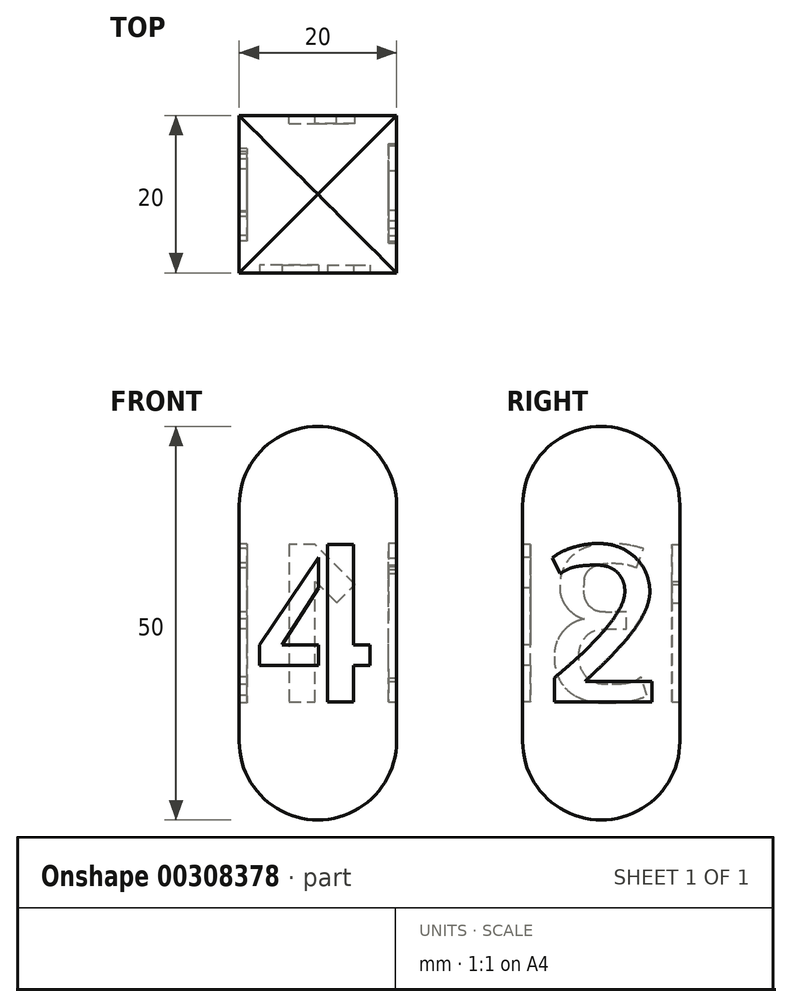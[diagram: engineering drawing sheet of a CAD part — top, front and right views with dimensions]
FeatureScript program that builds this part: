
annotation { "Feature Type Name" : "Feature", "Feature Type Description" : "" }
export const myFeature = defineFeature(function(context is Context, id is Id, definition is map)
    precondition{}
    {
        {
            var Q0;
            Q0=qCreatedBy(makeId("Top.planeOp"),FACE);
            var sketch = newSketch(context, id + "F0", { "sketchPlane" : qUnion([Q0])});
            skLineSegment(sketch, "E0.bottom", {"start": v(0, 0) * mm, "end": v(-20, 0) * mm});
            skLineSegment(sketch, "E0.top", {"start": v(0, 20) * mm, "end": v(-20, 20) * mm});
            skLineSegment(sketch, "E0.left", {"start": v(0, 0) * mm, "end": v(0, 20) * mm});
            skLineSegment(sketch, "E0.right", {"start": v(-20, 0) * mm, "end": v(-20, 20) * mm});
            skSolve(sketch);
        }
        {
            var Q0;
            Q0=makeQuery(id+"F0.imprint","IMPRINT",FACE,{"disambiguationData":[TD([[makeQuery(id+"F0.imprint","IMPRINT",EDGE,{"derivedFrom":sQuery(id+"F0.wireOp",EDGE,"E0.bottom")}),-1.0]])]});
            extrude(context, id + "F1", {"entities" : qUnion([Q0]), "depth" : 50 * mm});
        }
        {
            var Q0;
            Q0=makeQuery(id+"F1.opExtrude","CAP_EDGE",EDGE,{"disambiguationData":[OSD([sQuery(id+"F0.wireOp",EDGE,"E0.top")])],"isStart":false});
            var Q1;
            Q1=makeQuery(id+"F1.opExtrude","CAP_EDGE",EDGE,{"disambiguationData":[OSD([sQuery(id+"F0.wireOp",EDGE,"E0.bottom")])],"isStart":false});
            var Q2;
            Q2=makeQuery(id+"F1.opExtrude","CAP_EDGE",EDGE,{"disambiguationData":[OSD([sQuery(id+"F0.wireOp",EDGE,"E0.right")])],"isStart":false});
            var Q3;
            Q3=makeQuery(id+"F1.opExtrude","CAP_EDGE",EDGE,{"disambiguationData":[OSD([sQuery(id+"F0.wireOp",EDGE,"E0.left")])],"isStart":false});
            fillet(context, id + "F2", {"entities" : qUnion([Q0, Q1, Q2, Q3]), "radius" : 10 * mm, "tangentPropagation" : true, "allowEdgeOverflow" : false});
        }
        {
            var Q0;
            Q0=makeQuery(id+"F1.opExtrude","CAP_EDGE",EDGE,{"disambiguationData":[OSD([sQuery(id+"F0.wireOp",EDGE,"E0.bottom")])],"isStart":true});
            var Q1;
            Q1=makeQuery(id+"F1.opExtrude","CAP_EDGE",EDGE,{"disambiguationData":[OSD([sQuery(id+"F0.wireOp",EDGE,"E0.top")])],"isStart":true});
            var Q2;
            Q2=makeQuery(id+"F1.opExtrude","CAP_EDGE",EDGE,{"disambiguationData":[OSD([sQuery(id+"F0.wireOp",EDGE,"E0.left")])],"isStart":true});
            var Q3;
            Q3=makeQuery(id+"F1.opExtrude","CAP_EDGE",EDGE,{"disambiguationData":[OSD([sQuery(id+"F0.wireOp",EDGE,"E0.right")])],"isStart":true});
            fillet(context, id + "F3", {"entities" : qUnion([Q0, Q1, Q2, Q3]), "radius" : 10 * mm, "tangentPropagation" : true, "allowEdgeOverflow" : false});
        }
        {
            var Q0;
            Q0=makeQuery(id+"F1.opExtrude","SWEPT_FACE",FACE,{"disambiguationData":[OSD([sQuery(id+"F0.wireOp",EDGE,"E0.top")])]});
            var sketch = newSketch(context, id + "F4", { "sketchPlane" : qUnion([Q0])});
            skText(sketch, "E1", { "text": "1", "fontName": "AllertaStencil-Regular.ttf"});
            skLineSegment(sketch, "E2", {"start": v(0, 15) * mm, "end": v(20, 15) * mm, "construction": true});
            skLineSegment(sketch, "E3", {"start": v(3.95, 10) * mm, "end": v(3.95, 15) * mm, "construction": true});
            skLineSegment(sketch, "E4", {"start": v(0, 35) * mm, "end": v(20, 35) * mm, "construction": true});
            skLineSegment(sketch, "E5", {"start": v(3.05, 35) * mm, "end": v(3.05, 40) * mm, "construction": true});
            skLineSegment(sketch, "E6", {"start": v(15.51, 25) * mm, "end": v(20, 25) * mm, "construction": true});
            skLineSegment(sketch, "E7", {"start": v(4.49, 25.65) * mm, "end": v(0, 25.65) * mm, "construction": true});
            const initialGuessF4  = {"E1": [0.00449, 0.015, 1, 0, 0.02]};
            skSetInitialGuess(sketch, initialGuessF4);
            skSolve(sketch);
        }
        {
            var Q0;
            Q0=makeQuery(id+"F1.opExtrude","SWEPT_FACE",FACE,{"disambiguationData":[OSD([sQuery(id+"F0.wireOp",EDGE,"E0.left")])]});
            var sketch = newSketch(context, id + "F5", { "sketchPlane" : qUnion([Q0])});
            skLineSegment(sketch, "E8", {"start": v(20, 15) * mm, "end": v(0, 15) * mm, "construction": true});
            skLineSegment(sketch, "E9", {"start": v(20, 35) * mm, "end": v(0, 35) * mm, "construction": true});
            skLineSegment(sketch, "E10", {"start": v(10, 10) * mm, "end": v(10, 15) * mm, "construction": true});
            skLineSegment(sketch, "E11", {"start": v(9, 40) * mm, "end": v(9, 35) * mm, "construction": true});
            skText(sketch, "E12", { "text": "2", "fontName": "AllertaStencil-Regular.ttf"});
            skLineSegment(sketch, "E13", {"start": v(18.32, 25.83) * mm, "end": v(20, 25.83) * mm, "construction": true});
            skLineSegment(sketch, "E14", {"start": v(0, 25.73) * mm, "end": v(1.68, 25.73) * mm, "construction": true});
            skPoint(sketch, "E14.endSnap0", {"position": v(1.68, 25) * mm});
            const initialGuessF5  = {"E12": [0.00168, 0.015, 1, 0, 0.02]};
            skSetInitialGuess(sketch, initialGuessF5);
            skSolve(sketch);
        }
        {
            var Q0;
            Q0=makeQuery(id+"F1.opExtrude","SWEPT_FACE",FACE,{"disambiguationData":[OSD([sQuery(id+"F0.wireOp",EDGE,"E0.bottom")])]});
            var sketch = newSketch(context, id + "F6", { "sketchPlane" : qUnion([Q0])});
            skLineSegment(sketch, "E15", {"start": v(-20, 35) * mm, "end": v(0, 35) * mm, "construction": true});
            skLineSegment(sketch, "E16", {"start": v(-20, 15) * mm, "end": v(0, 15) * mm, "construction": true});
            skLineSegment(sketch, "E17", {"start": v(-10, 35) * mm, "end": v(-10, 40) * mm, "construction": true});
            skLineSegment(sketch, "E18", {"start": v(-10, 10) * mm, "end": v(-10, 15) * mm, "construction": true});
            skText(sketch, "E19", { "text": "4", "fontName": "AllertaStencil-Regular.ttf"});
            skLineSegment(sketch, "E20", {"start": v(-1.53, 25) * mm, "end": v(0, 25) * mm, "construction": true});
            skLineSegment(sketch, "E21", {"start": v(-18.47, 25.61) * mm, "end": v(-20, 25.61) * mm, "construction": true});
            const initialGuessF6  = {"E19": [-0.01847, 0.015, 1, 0, 0.02]};
            skSetInitialGuess(sketch, initialGuessF6);
            skSolve(sketch);
        }
        {
            var Q0;
            Q0=makeQuery(id+"F1.opExtrude","SWEPT_FACE",FACE,{"disambiguationData":[OSD([sQuery(id+"F0.wireOp",EDGE,"E0.right")])]});
            var sketch = newSketch(context, id + "F7", { "sketchPlane" : qUnion([Q0])});
            skLineSegment(sketch, "E22", {"start": v(-20, 15) * mm, "end": v(0, 15) * mm, "construction": true});
            skLineSegment(sketch, "E23", {"start": v(0, 35) * mm, "end": v(-20, 35) * mm, "construction": true});
            skLineSegment(sketch, "E24", {"start": v(-11.24, 40) * mm, "end": v(-11.24, 35) * mm, "construction": true});
            skLineSegment(sketch, "E25", {"start": v(-12.04, 10) * mm, "end": v(-12.04, 15) * mm, "construction": true});
            skText(sketch, "E26", { "text": "3", "fontName": "AllertaStencil-Regular.ttf"});
            skLineSegment(sketch, "E27", {"start": v(-2.17, 25) * mm, "end": v(0, 25) * mm, "construction": true});
            skLineSegment(sketch, "E28", {"start": v(-17.83, 25.74) * mm, "end": v(-20, 25.74) * mm, "construction": true});
            const initialGuessF7  = {"E26": [-0.01783, 0.015, 1, 0, 0.02]};
            skSetInitialGuess(sketch, initialGuessF7);
            skSolve(sketch);
        }
        {
            var Q0;
            Q0 = qSketchRegion(id + "F4", true);
            extrude(context, id + "F8", {"entities" : qUnion([Q0]), "operationType" : NewBodyOperationType.REMOVE, "oppositeDirection" : true, "depth" : 1 * mm});
        }
        {
            var Q0;
            Q0 = qSketchRegion(id + "F5", true);
            extrude(context, id + "F9", {"entities" : qUnion([Q0]), "operationType" : NewBodyOperationType.REMOVE, "oppositeDirection" : true, "depth" : 1 * mm});
        }
        {
            var Q0;
            Q0 = qSketchRegion(id + "F6", true);
            extrude(context, id + "F10", {"entities" : qUnion([Q0]), "operationType" : NewBodyOperationType.REMOVE, "oppositeDirection" : true, "depth" : 1 * mm});
        }
        {
            var Q0;
            Q0 = qSketchRegion(id + "F7", true);
            extrude(context, id + "F11", {"entities" : qUnion([Q0]), "operationType" : NewBodyOperationType.REMOVE, "oppositeDirection" : true, "depth" : 1 * mm});
        }
    });
